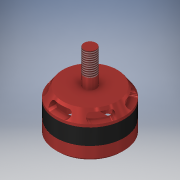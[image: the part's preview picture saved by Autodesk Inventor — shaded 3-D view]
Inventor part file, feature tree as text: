
AUTODESK INVENTOR PART (.ipt)
format: ipt  version: 2019.3 (Build 233278000, 278)  size: 404,480 bytes
history: native  units: mm
features: sketch x8, extrude x5, plane x4, revolve x2, pattern_circular x2, split x2, other x2, projected_geometry x2, shell x1, thread x1, chamfer x1, hole x1
ambient origin geometry x8: Origin, YZ Plane, XZ Plane, XY Plane, X Axis, Y Axis, Z Axis, Center Point
bodies: Solid1 (feature_tree)
feature tree (31):
  revolve  "Revolution1"  [1 undecoded]
  shell  "Shell1"  Thickness=22.5mm
  extrude  "Extrusion1"  TaperAngle=90.0deg  [1 undecoded]
  thread  "Thread1"  [1 undecoded]
  plane  "Work Plane1"
  extrude  "Extrusion2"  Depth=14.0mm TaperAngle=0.0deg
  pattern_circular  "Circular Pattern1"  [2 undecoded]
  plane  "Work Plane3"
  split  "Split1"
  split  "Split2"
  extrude  "Extrusion3"  Depth=2.0mm TaperAngle=360.0deg
  pattern_circular  "Circular Pattern2"  [2 undecoded]
  extrude  "Extrusion4"  Depth=3.5mm
  revolve  "Revolution2"  [1 undecoded]
  sketch  "Sketch7"  dims[d16=1.0mm]
  plane  "Work Plane4"
  chamfer  "Chamfer1"  Distance=2.5mm
  extrude  "Extrusion6"  Depth=2.0mm
  hole  "Hole1"  [1 undecoded]
  sketch  "Sketch1"  dims[d0=17.2mm d1=28.0mm d2=22.5mm]
  sketch  "Sketch2"  dims[d3=13.2mm d4=90.0deg d5=5.0mm]
  sketch  "Sketch3"  dims[d6=14.0mm d7=0.0mm d8=9.5mm d9=0.0mm]
  plane  "Work Plane2"
  sketch  "Sketch4"  dims[d10=1.0mm d11=2.5mm]
  sketch  "Sketch5"  dims[d13=5.8mm]
  sketch  "Sketch6"  dims[d14=9.0mm d15=0.0mm]
  sketch  "Sketch8"  dims[d17=4.0mm d18=13.2mm d19=60.0mm d20=360.0deg d22=-5.5mm d23=-6.6mm d24=3.5mm d25=5.0mm d27=2.5mm d28=8.42mm d29=4.0mm d30=0.0mm d31=40.0mm d32=360.0deg d34=8.0mm d35=2.0mm d36=0.0mm d37=1.0mm d38=90.0deg d40=90.0deg d41=45.0deg d42=4.5mm d43=2.5mm d44=2.5mm d45=6.0mm d48=-14.0mm d49=1.0mm d50=2.0mm d51=45.0deg d52=9.0mm d53=3.5mm d54=2.0mm d55=0.0mm d56=2.459mm d57=6.0mm d58=6.5mm d59=3.4mm d60=90.0deg d61=8.8mm d62=20.594885mm]
  other  "Motor_Bottom"
  other  "Motor_Top"
  projected_geometry  "Project Cut Edges1"
  projected_geometry  "Project Cut Edges2"
note: 9 required parameter values undecoded (feature->parameter linkage not recoverable at this tier; creation-order binding heuristic only, values carry confidence <= 0.55)